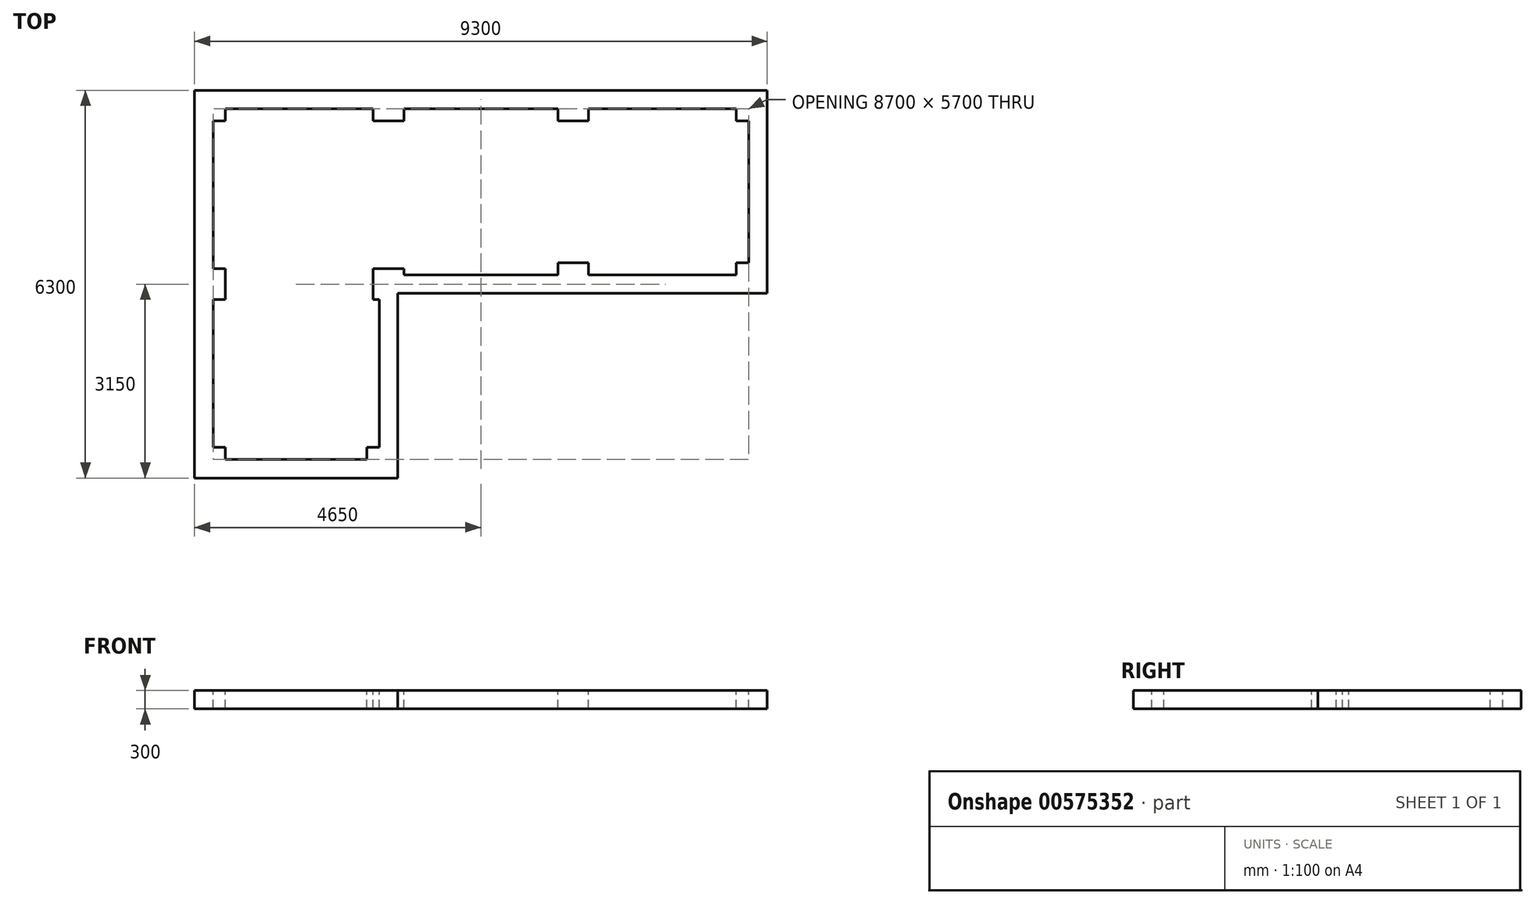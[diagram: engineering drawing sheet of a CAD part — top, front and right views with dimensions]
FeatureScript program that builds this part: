
annotation { "Feature Type Name" : "Feature", "Feature Type Description" : "" }
export const myFeature = defineFeature(function(context is Context, id is Id, definition is map)
    precondition{}
    {
        {
            var Q0;
            Q0=qCreatedBy(makeId("Top.planeOp"),FACE);
            var sketch = newSketch(context, id + "F0", { "sketchPlane" : qUnion([Q0])});
            skLineSegment(sketch, "E0", {"start": v(-3732.08, -3000) * mm, "end": v(-3732.08, 3000) * mm, "construction": true});
            skLineSegment(sketch, "E1", {"start": v(-3732.08, 3000) * mm, "end": v(5267.92, 3000) * mm, "construction": true});
            skLineSegment(sketch, "E2", {"start": v(5267.92, 3000) * mm, "end": v(5267.92, 0) * mm, "construction": true});
            skLineSegment(sketch, "E3", {"start": v(-732.08, -3000) * mm, "end": v(-732.08, 0) * mm, "construction": true});
            skPoint(sketch, "E4.middle", {"position": v(-3732.08, 3000) * mm});
            skPoint(sketch, "E5.middle", {"position": v(-3732.08, -3000) * mm});
            skPoint(sketch, "E6.middle", {"position": v(5267.92, 0) * mm});
            skPoint(sketch, "E7.middle", {"position": v(5267.92, 3000) * mm});
            skPoint(sketch, "E8", {"position": v(-732.08, 3000) * mm});
            skPoint(sketch, "E9", {"position": v(2267.92, 3000) * mm});
            skPoint(sketch, "E10", {"position": v(-3732.08, 0) * mm});
            skPoint(sketch, "E11.middle", {"position": v(-732.08, 0) * mm});
            skPoint(sketch, "E12.middle", {"position": v(-732.08, -3000) * mm});
            skLineSegment(sketch, "E13", {"start": v(-3732.08, -3000) * mm, "end": v(-732.08, -3000) * mm, "construction": true});
            skLineSegment(sketch, "E14", {"start": v(-732.08, 0) * mm, "end": v(5267.92, 0) * mm, "construction": true});
            skLineSegment(sketch, "E15", {"start": v(-3882.08, 3150) * mm, "end": v(-3882.08, -3150) * mm});
            skLineSegment(sketch, "E16", {"start": v(-582.08, -3150) * mm, "end": v(-3882.08, -3150) * mm});
            skLineSegment(sketch, "E17", {"start": v(-3882.08, 3150) * mm, "end": v(5417.92, 3150) * mm});
            skLineSegment(sketch, "E18", {"start": v(5417.92, 3150) * mm, "end": v(5417.92, -150) * mm});
            skLineSegment(sketch, "E19", {"start": v(5417.92, -150) * mm, "end": v(-582.08, -150) * mm});
            skLineSegment(sketch, "E20.trimOffspring", {"start": v(-582.08, -150) * mm, "end": v(-582.08, -3150) * mm});
            skLineSegment(sketch, "E21.0", {"start": v(-3382.08, 2850) * mm, "end": v(-982.08, 2850) * mm});
            skLineSegment(sketch, "E22.0", {"start": v(5117.92, 2650) * mm, "end": v(5117.92, 350) * mm});
            skLineSegment(sketch, "E23.0", {"start": v(4917.92, 150) * mm, "end": v(2517.92, 150) * mm});
            skLineSegment(sketch, "E24.0", {"start": v(-882.08, -250) * mm, "end": v(-882.08, -2650) * mm});
            skLineSegment(sketch, "E25.trimOffspring", {"start": v(-1082.08, -2850) * mm, "end": v(-3382.08, -2850) * mm});
            skLineSegment(sketch, "E26.trimOffspring", {"start": v(-3582.08, 2650) * mm, "end": v(-3582.08, 250) * mm});
            skPoint(sketch, "E27", {"position": v(2267.92, 0) * mm});
            skLineSegment(sketch, "E28", {"start": v(-3582.08, 2650) * mm, "end": v(-3382.08, 2650) * mm});
            skLineSegment(sketch, "E29", {"start": v(-3382.08, 2650) * mm, "end": v(-3382.08, 2850) * mm});
            skLineSegment(sketch, "E30", {"start": v(-982.08, 2650) * mm, "end": v(-482.08, 2650) * mm});
            skLineSegment(sketch, "E31", {"start": v(-482.08, 2650) * mm, "end": v(-482.08, 2850) * mm});
            skLineSegment(sketch, "E32.trimOffspring", {"start": v(-482.08, 2850) * mm, "end": v(2017.92, 2850) * mm});
            skLineSegment(sketch, "E33.trimOffspring", {"start": v(-982.08, 2850) * mm, "end": v(-982.08, 2650) * mm});
            skPoint(sketch, "E34.start.orphan", {"position": v(-982.08, 3150) * mm});
            skLineSegment(sketch, "E35", {"start": v(2017.92, 2650) * mm, "end": v(2517.92, 2650) * mm});
            skLineSegment(sketch, "E36", {"start": v(2517.92, 2650) * mm, "end": v(2517.92, 2850) * mm});
            skLineSegment(sketch, "E37.trimOffspring", {"start": v(2517.92, 2850) * mm, "end": v(4917.92, 2850) * mm});
            skLineSegment(sketch, "E38.trimOffspring", {"start": v(2017.92, 2850) * mm, "end": v(2017.92, 2650) * mm});
            skLineSegment(sketch, "E39", {"start": v(5117.92, 2650) * mm, "end": v(4917.92, 2650) * mm});
            skLineSegment(sketch, "E40", {"start": v(4917.92, 2650) * mm, "end": v(4917.92, 2850) * mm});
            skLineSegment(sketch, "E41", {"start": v(4917.92, 350) * mm, "end": v(4917.92, 150) * mm});
            skLineSegment(sketch, "E42", {"start": v(2017.92, 350) * mm, "end": v(2517.92, 350) * mm});
            skLineSegment(sketch, "E43", {"start": v(2517.92, 350) * mm, "end": v(2517.92, 150) * mm});
            skLineSegment(sketch, "E44", {"start": v(-982.08, -250) * mm, "end": v(-982.08, 250) * mm});
            skLineSegment(sketch, "E45", {"start": v(-982.08, 250) * mm, "end": v(-482.08, 250) * mm});
            skLineSegment(sketch, "E46", {"start": v(-482.08, 250) * mm, "end": v(-482.08, 150) * mm});
            skLineSegment(sketch, "E47.trimOffspring", {"start": v(-882.08, -250) * mm, "end": v(-982.08, -250) * mm});
            skLineSegment(sketch, "E48.trimOffspring", {"start": v(2017.92, 150) * mm, "end": v(2017.92, 350) * mm});
            skLineSegment(sketch, "E49.trimOffspring", {"start": v(2017.92, 150) * mm, "end": v(-482.08, 150) * mm});
            skLineSegment(sketch, "E50.trimOffspring", {"start": v(5117.92, 350) * mm, "end": v(4917.92, 350) * mm});
            skLineSegment(sketch, "E51", {"start": v(-3382.08, -2650) * mm, "end": v(-3382.08, -2850) * mm});
            skLineSegment(sketch, "E52", {"start": v(-1082.08, -2650) * mm, "end": v(-882.08, -2650) * mm});
            skLineSegment(sketch, "E53.trimOffspring", {"start": v(-3582.08, -2650) * mm, "end": v(-3382.08, -2650) * mm});
            skLineSegment(sketch, "E54.trimOffspring", {"start": v(-1082.08, -2850) * mm, "end": v(-1082.08, -2650) * mm});
            skLineSegment(sketch, "E55", {"start": v(-3582.08, 250) * mm, "end": v(-3382.08, 250) * mm});
            skLineSegment(sketch, "E56", {"start": v(-3382.08, 250) * mm, "end": v(-3382.08, -250) * mm});
            skLineSegment(sketch, "E57", {"start": v(-3382.08, -250) * mm, "end": v(-3582.08, -250) * mm});
            skLineSegment(sketch, "E58.trimOffspring", {"start": v(-3582.08, -250) * mm, "end": v(-3582.08, -2650) * mm});
            skSolve(sketch);
        }
        {
            var Q0;
            Q0=makeQuery(id+"F0.imprint","IMPRINT",FACE,{"disambiguationData":[TD([[makeQuery(id+"F0.imprint","IMPRINT",EDGE,{"derivedFrom":sQuery(id+"F0.wireOp",EDGE,"E15")}),1.0]])]});
            extrude(context, id + "F1", {"entities" : qUnion([Q0]), "oppositeDirection" : true, "depth" : 300 * mm});
        }
    });
